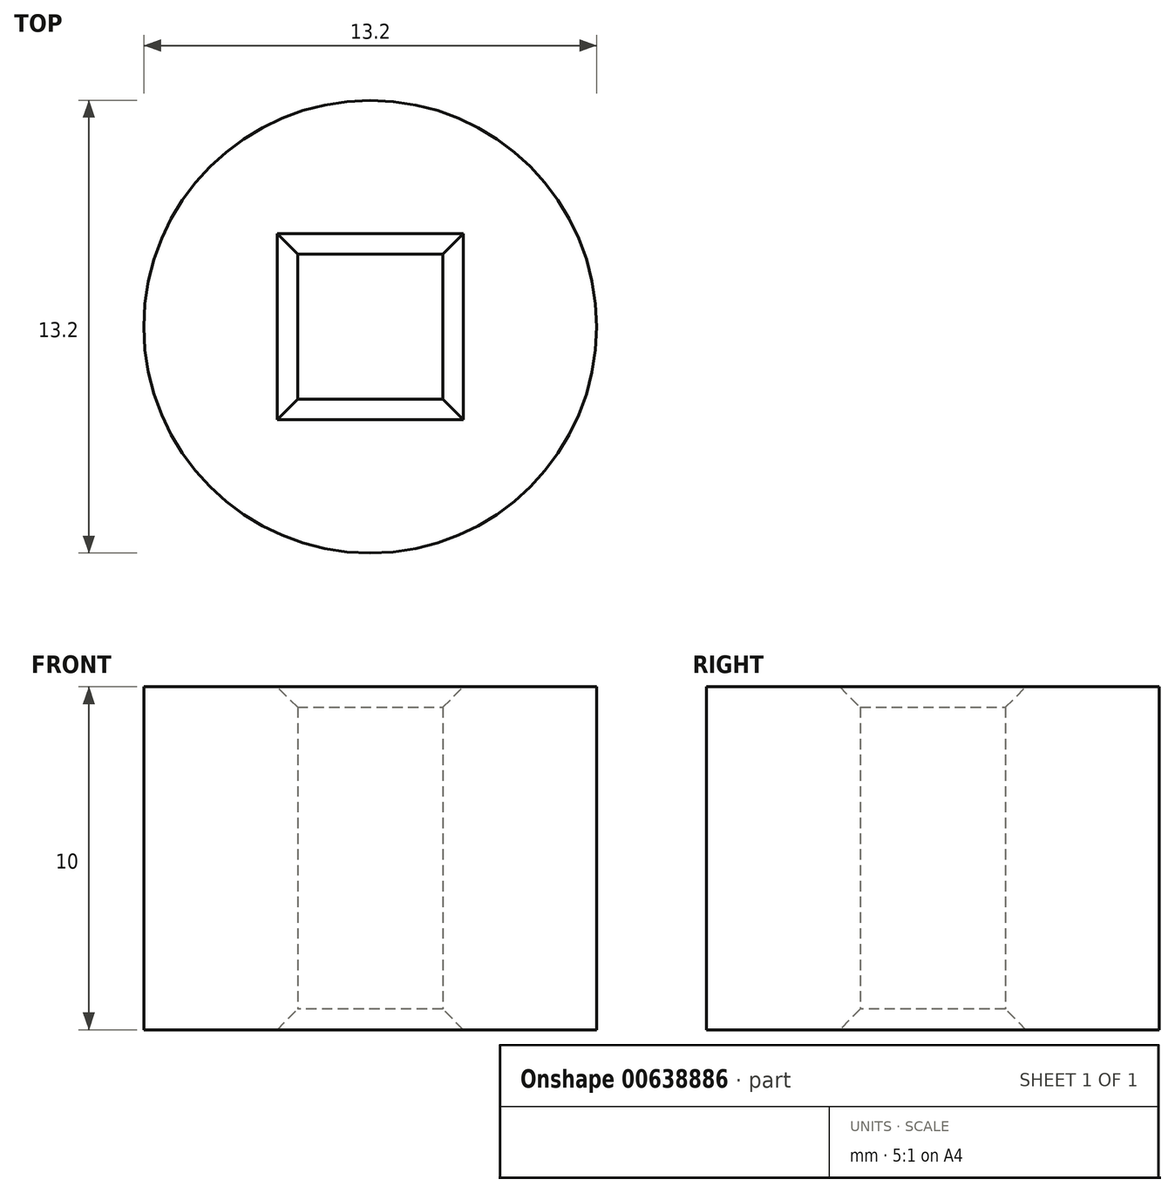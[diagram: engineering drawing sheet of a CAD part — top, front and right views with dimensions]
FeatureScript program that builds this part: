
annotation { "Feature Type Name" : "Feature", "Feature Type Description" : "" }
export const myFeature = defineFeature(function(context is Context, id is Id, definition is map)
    precondition{}
    {
        {
            var Q0;
            Q0=qCreatedBy(makeId("Top.planeOp"),FACE);
            var sketch = newSketch(context, id + "F0", { "sketchPlane" : qUnion([Q0])});
            skLineSegment(sketch, "E0.bottom", {"start": v(15, -7.37) * mm, "end": v(-15, -7.37) * mm, "construction": true});
            skLineSegment(sketch, "E0.top", {"start": v(15, 7.37) * mm, "end": v(-15, 7.37) * mm, "construction": true});
            skLineSegment(sketch, "E0.left", {"start": v(15, -7.37) * mm, "end": v(15, 7.37) * mm, "construction": true});
            skLineSegment(sketch, "E0.right", {"start": v(-15, -7.37) * mm, "end": v(-15, 7.37) * mm, "construction": true});
            skPoint(sketch, "E0.middle", {"position": v(0, 0) * mm});
            skCircle(sketch, "E1", {"center": v(-15, 7.37) * mm, "radius": 6.6 * mm});
            skCircle(sketch, "E2", {"center": v(-15, -7.37) * mm, "radius": 6.1 * mm});
            skCircle(sketch, "E3", {"center": v(15, -7.37) * mm, "radius": 4.85 * mm});
            skCircle(sketch, "E4", {"center": v(15, 7.37) * mm, "radius": 5.35 * mm});
            skCircle(sketch, "E5", {"center": v(0, 0) * mm, "radius": 7.1 * mm});
            skLineSegment(sketch, "E6.bottom", {"start": v(-12.88, 5.25) * mm, "end": v(-17.12, 5.25) * mm});
            skLineSegment(sketch, "E6.top", {"start": v(-12.88, 9.48) * mm, "end": v(-17.12, 9.48) * mm});
            skLineSegment(sketch, "E6.left", {"start": v(-12.88, 5.25) * mm, "end": v(-12.88, 9.48) * mm});
            skLineSegment(sketch, "E6.right", {"start": v(-17.12, 5.25) * mm, "end": v(-17.12, 9.48) * mm});
            skLineSegment(sketch, "E7.bottom", {"start": v(-12.88, -9.48) * mm, "end": v(-17.12, -9.48) * mm});
            skLineSegment(sketch, "E7.top", {"start": v(-12.88, -5.25) * mm, "end": v(-17.12, -5.25) * mm});
            skLineSegment(sketch, "E7.left", {"start": v(-12.88, -9.48) * mm, "end": v(-12.88, -5.25) * mm});
            skLineSegment(sketch, "E7.right", {"start": v(-17.12, -9.48) * mm, "end": v(-17.12, -5.25) * mm});
            skLineSegment(sketch, "E8.bottom", {"start": v(2.12, -2.11) * mm, "end": v(-2.12, -2.12) * mm});
            skLineSegment(sketch, "E8.top", {"start": v(2.11, 2.12) * mm, "end": v(-2.12, 2.12) * mm});
            skLineSegment(sketch, "E8.left", {"start": v(2.12, -2.11) * mm, "end": v(2.11, 2.12) * mm});
            skLineSegment(sketch, "E8.right", {"start": v(-2.12, -2.12) * mm, "end": v(-2.12, 2.12) * mm});
            skLineSegment(sketch, "E9.left", {"start": v(17.02, 2.41) * mm, "end": v(17.02, 7.81) * mm});
            skLineSegment(sketch, "E10.bottom", {"start": v(17.12, -9.48) * mm, "end": v(12.89, -9.48) * mm});
            skLineSegment(sketch, "E10.top", {"start": v(17.12, -5.25) * mm, "end": v(12.88, -5.25) * mm});
            skLineSegment(sketch, "E10.left", {"start": v(17.12, -9.48) * mm, "end": v(17.12, -5.25) * mm});
            skLineSegment(sketch, "E10.right", {"start": v(12.89, -9.48) * mm, "end": v(12.88, -5.25) * mm});
            skLineSegment(sketch, "E11.bottom", {"start": v(17.12, 5.25) * mm, "end": v(12.88, 5.25) * mm});
            skLineSegment(sketch, "E11.top", {"start": v(17.12, 9.48) * mm, "end": v(12.88, 9.48) * mm});
            skLineSegment(sketch, "E11.left", {"start": v(17.12, 5.25) * mm, "end": v(17.12, 9.48) * mm});
            skLineSegment(sketch, "E11.right", {"start": v(12.88, 5.25) * mm, "end": v(12.88, 9.48) * mm});
            skLineSegment(sketch, "E12.bottom", {"start": v(19, -11) * mm, "end": v(-19, -11) * mm});
            skLineSegment(sketch, "E12.top", {"start": v(19, 11) * mm, "end": v(-19, 11) * mm});
            skLineSegment(sketch, "E12.left", {"start": v(19, -11) * mm, "end": v(19, 11) * mm});
            skLineSegment(sketch, "E12.right", {"start": v(-19, -11) * mm, "end": v(-19, 11) * mm});
            skLineSegment(sketch, "E13.bottom", {"start": v(18.6, -10.6) * mm, "end": v(-18.6, -10.6) * mm});
            skLineSegment(sketch, "E13.top", {"start": v(18.6, 10.6) * mm, "end": v(-18.6, 10.6) * mm});
            skLineSegment(sketch, "E13.left", {"start": v(18.6, -10.6) * mm, "end": v(18.6, 10.6) * mm});
            skLineSegment(sketch, "E13.right", {"start": v(-18.6, -10.6) * mm, "end": v(-18.6, 10.6) * mm});
            skSolve(sketch);
        }
        {
            var Q0;
            Q0=makeQuery(id+"F0.imprint","IMPRINT",FACE,{"disambiguationData":[TD([[makeQuery(id+"F0.imprint","IMPRINT",EDGE,{"derivedFrom":sQuery(id+"F0.wireOp",EDGE,"E1")}),1.0]])]});
            var Q1;
            {var subQ0=sQuery(id+"F0.wireOp",EDGE,"E12.top");var subQ1=sQuery(id+"F0.wireOp",EDGE,"E1");var subQ2=makeQuery(id+"F0.imprint","INTERSECT",VERTEX,{"derivedFrom":[subQ1,subQ0]});Q1=makeQuery(id+"F0.imprint","IMPRINT",FACE,{"disambiguationData":[TD([[makeQuery(id+"F0.imprint","IMPRINT",EDGE,{"disambiguationData":[TD([[subQ2,-1.0]])],"derivedFrom":subQ1}),1.0]])]});}
            var Q2;
            Q2=makeQuery(id+"F0.imprint","IMPRINT",FACE,{"disambiguationData":[TD([[makeQuery(id+"F0.imprint","IMPRINT",EDGE,{"derivedFrom":sQuery(id+"F0.wireOp",EDGE,"E6.bottom")}),1.0]])]});
            extrude(context, id + "F1", {"entities" : qUnion([Q0, Q1, Q2]), "depth" : 10 * mm, "offsetDistance" : 25 * mm});
        }
        {
            var Q0;
            Q0=makeQuery(id+"F1.opExtrude","CAP_EDGE",EDGE,{"disambiguationData":[OSD([sQuery(id+"F0.wireOp",EDGE,"E8.right")])],"isStart":false});
            var Q1;
            Q1=makeQuery(id+"F1.opExtrude","CAP_EDGE",EDGE,{"disambiguationData":[OSD([sQuery(id+"F0.wireOp",EDGE,"E8.bottom")])],"isStart":false});
            var Q2;
            Q2=makeQuery(id+"F1.opExtrude","CAP_EDGE",EDGE,{"disambiguationData":[OSD([sQuery(id+"F0.wireOp",EDGE,"E8.top")])],"isStart":false});
            var Q3;
            Q3=makeQuery(id+"F1.opExtrude","CAP_EDGE",EDGE,{"disambiguationData":[OSD([sQuery(id+"F0.wireOp",EDGE,"E8.left")])],"isStart":false});
            var Q4;
            Q4=makeQuery(id+"F1.opExtrude","CAP_EDGE",EDGE,{"disambiguationData":[OSD([sQuery(id+"F0.wireOp",EDGE,"E10.right")])],"isStart":false});
            var Q5;
            Q5=makeQuery(id+"F1.opExtrude","CAP_EDGE",EDGE,{"disambiguationData":[OSD([sQuery(id+"F0.wireOp",EDGE,"E10.top")])],"isStart":false});
            var Q6;
            Q6=makeQuery(id+"F1.opExtrude","CAP_EDGE",EDGE,{"disambiguationData":[OSD([sQuery(id+"F0.wireOp",EDGE,"E10.left")])],"isStart":false});
            var Q7;
            Q7=makeQuery(id+"F1.opExtrude","CAP_EDGE",EDGE,{"disambiguationData":[OSD([sQuery(id+"F0.wireOp",EDGE,"E10.bottom")])],"isStart":false});
            var Q8;
            Q8=makeQuery(id+"F1.opExtrude","CAP_EDGE",EDGE,{"disambiguationData":[OSD([sQuery(id+"F0.wireOp",EDGE,"E11.right")])],"isStart":false});
            var Q9;
            Q9=makeQuery(id+"F1.opExtrude","CAP_EDGE",EDGE,{"disambiguationData":[OSD([sQuery(id+"F0.wireOp",EDGE,"E11.top")])],"isStart":false});
            var Q10;
            Q10=makeQuery(id+"F1.opExtrude","CAP_EDGE",EDGE,{"disambiguationData":[OSD([sQuery(id+"F0.wireOp",EDGE,"E11.bottom")])],"isStart":false});
            var Q11;
            Q11=makeQuery(id+"F1.opExtrude","CAP_EDGE",EDGE,{"disambiguationData":[OSD([sQuery(id+"F0.wireOp",EDGE,"E11.left")])],"isStart":false});
            var Q12;
            Q12=makeQuery(id+"F1.opExtrude","CAP_EDGE",EDGE,{"disambiguationData":[OSD([sQuery(id+"F0.wireOp",EDGE,"E7.right")])],"isStart":false});
            var Q13;
            Q13=makeQuery(id+"F1.opExtrude","CAP_EDGE",EDGE,{"disambiguationData":[OSD([sQuery(id+"F0.wireOp",EDGE,"E7.bottom")])],"isStart":false});
            var Q14;
            Q14=makeQuery(id+"F1.opExtrude","CAP_EDGE",EDGE,{"disambiguationData":[OSD([sQuery(id+"F0.wireOp",EDGE,"E7.top")])],"isStart":false});
            var Q15;
            Q15=makeQuery(id+"F1.opExtrude","CAP_EDGE",EDGE,{"disambiguationData":[OSD([sQuery(id+"F0.wireOp",EDGE,"E7.left")])],"isStart":false});
            var Q16;
            Q16=makeQuery(id+"F1.opExtrude","CAP_EDGE",EDGE,{"disambiguationData":[OSD([sQuery(id+"F0.wireOp",EDGE,"E6.right")])],"isStart":false});
            var Q17;
            Q17=makeQuery(id+"F1.opExtrude","CAP_EDGE",EDGE,{"disambiguationData":[OSD([sQuery(id+"F0.wireOp",EDGE,"E6.bottom")])],"isStart":false});
            var Q18;
            Q18=makeQuery(id+"F1.opExtrude","CAP_EDGE",EDGE,{"disambiguationData":[OSD([sQuery(id+"F0.wireOp",EDGE,"E6.left")])],"isStart":false});
            var Q19;
            Q19=makeQuery(id+"F1.opExtrude","CAP_EDGE",EDGE,{"disambiguationData":[OSD([sQuery(id+"F0.wireOp",EDGE,"E6.top")])],"isStart":false});
            chamfer(context, id + "F2", {"entities" : qUnion([Q0, Q1, Q2, Q3, Q4, Q5, Q6, Q7, Q8, Q9, Q10, Q11, Q12, Q13, Q14, Q15, Q16, Q17, Q18, Q19]), "width" : .6 * mm, "tangentPropagation" : true});
        }
        {
            var Q0;
            Q0=makeQuery(id+"F1.opExtrude","CAP_EDGE",EDGE,{"disambiguationData":[OSD([sQuery(id+"F0.wireOp",EDGE,"E6.bottom")])],"isStart":true});
            var Q1;
            Q1=makeQuery(id+"F1.opExtrude","CAP_EDGE",EDGE,{"disambiguationData":[OSD([sQuery(id+"F0.wireOp",EDGE,"E6.right")])],"isStart":true});
            var Q2;
            Q2=makeQuery(id+"F1.opExtrude","CAP_EDGE",EDGE,{"disambiguationData":[OSD([sQuery(id+"F0.wireOp",EDGE,"E6.top")])],"isStart":true});
            var Q3;
            Q3=makeQuery(id+"F1.opExtrude","CAP_EDGE",EDGE,{"disambiguationData":[OSD([sQuery(id+"F0.wireOp",EDGE,"E6.left")])],"isStart":true});
            var Q4;
            Q4=makeQuery(id+"F1.opExtrude","CAP_EDGE",EDGE,{"disambiguationData":[OSD([sQuery(id+"F0.wireOp",EDGE,"E7.right")])],"isStart":true});
            var Q5;
            Q5=makeQuery(id+"F1.opExtrude","CAP_EDGE",EDGE,{"disambiguationData":[OSD([sQuery(id+"F0.wireOp",EDGE,"E7.bottom")])],"isStart":true});
            var Q6;
            Q6=makeQuery(id+"F1.opExtrude","CAP_EDGE",EDGE,{"disambiguationData":[OSD([sQuery(id+"F0.wireOp",EDGE,"E7.left")])],"isStart":true});
            var Q7;
            Q7=makeQuery(id+"F1.opExtrude","CAP_EDGE",EDGE,{"disambiguationData":[OSD([sQuery(id+"F0.wireOp",EDGE,"E7.top")])],"isStart":true});
            var Q8;
            Q8=makeQuery(id+"F1.opExtrude","CAP_EDGE",EDGE,{"disambiguationData":[OSD([sQuery(id+"F0.wireOp",EDGE,"E8.right")])],"isStart":true});
            var Q9;
            Q9=makeQuery(id+"F1.opExtrude","CAP_EDGE",EDGE,{"disambiguationData":[OSD([sQuery(id+"F0.wireOp",EDGE,"E8.bottom")])],"isStart":true});
            var Q10;
            Q10=makeQuery(id+"F1.opExtrude","CAP_EDGE",EDGE,{"disambiguationData":[OSD([sQuery(id+"F0.wireOp",EDGE,"E8.left")])],"isStart":true});
            var Q11;
            Q11=makeQuery(id+"F1.opExtrude","CAP_EDGE",EDGE,{"disambiguationData":[OSD([sQuery(id+"F0.wireOp",EDGE,"E8.top")])],"isStart":true});
            var Q12;
            Q12=makeQuery(id+"F1.opExtrude","CAP_EDGE",EDGE,{"disambiguationData":[OSD([sQuery(id+"F0.wireOp",EDGE,"E11.right")])],"isStart":true});
            var Q13;
            Q13=makeQuery(id+"F1.opExtrude","CAP_EDGE",EDGE,{"disambiguationData":[OSD([sQuery(id+"F0.wireOp",EDGE,"E11.bottom")])],"isStart":true});
            var Q14;
            Q14=makeQuery(id+"F1.opExtrude","CAP_EDGE",EDGE,{"disambiguationData":[OSD([sQuery(id+"F0.wireOp",EDGE,"E11.left")])],"isStart":true});
            var Q15;
            Q15=makeQuery(id+"F1.opExtrude","CAP_EDGE",EDGE,{"disambiguationData":[OSD([sQuery(id+"F0.wireOp",EDGE,"E11.top")])],"isStart":true});
            var Q16;
            Q16=makeQuery(id+"F1.opExtrude","CAP_EDGE",EDGE,{"disambiguationData":[OSD([sQuery(id+"F0.wireOp",EDGE,"E10.right")])],"isStart":true});
            var Q17;
            Q17=makeQuery(id+"F1.opExtrude","CAP_EDGE",EDGE,{"disambiguationData":[OSD([sQuery(id+"F0.wireOp",EDGE,"E10.bottom")])],"isStart":true});
            var Q18;
            Q18=makeQuery(id+"F1.opExtrude","CAP_EDGE",EDGE,{"disambiguationData":[OSD([sQuery(id+"F0.wireOp",EDGE,"E10.left")])],"isStart":true});
            var Q19;
            Q19=makeQuery(id+"F1.opExtrude","CAP_EDGE",EDGE,{"disambiguationData":[OSD([sQuery(id+"F0.wireOp",EDGE,"E10.top")])],"isStart":true});
            chamfer(context, id + "F3", {"entities" : qUnion([Q0, Q1, Q2, Q3, Q4, Q5, Q6, Q7, Q8, Q9, Q10, Q11, Q12, Q13, Q14, Q15, Q16, Q17, Q18, Q19]), "width" : .6 * mm, "tangentPropagation" : true});
        }
    });
